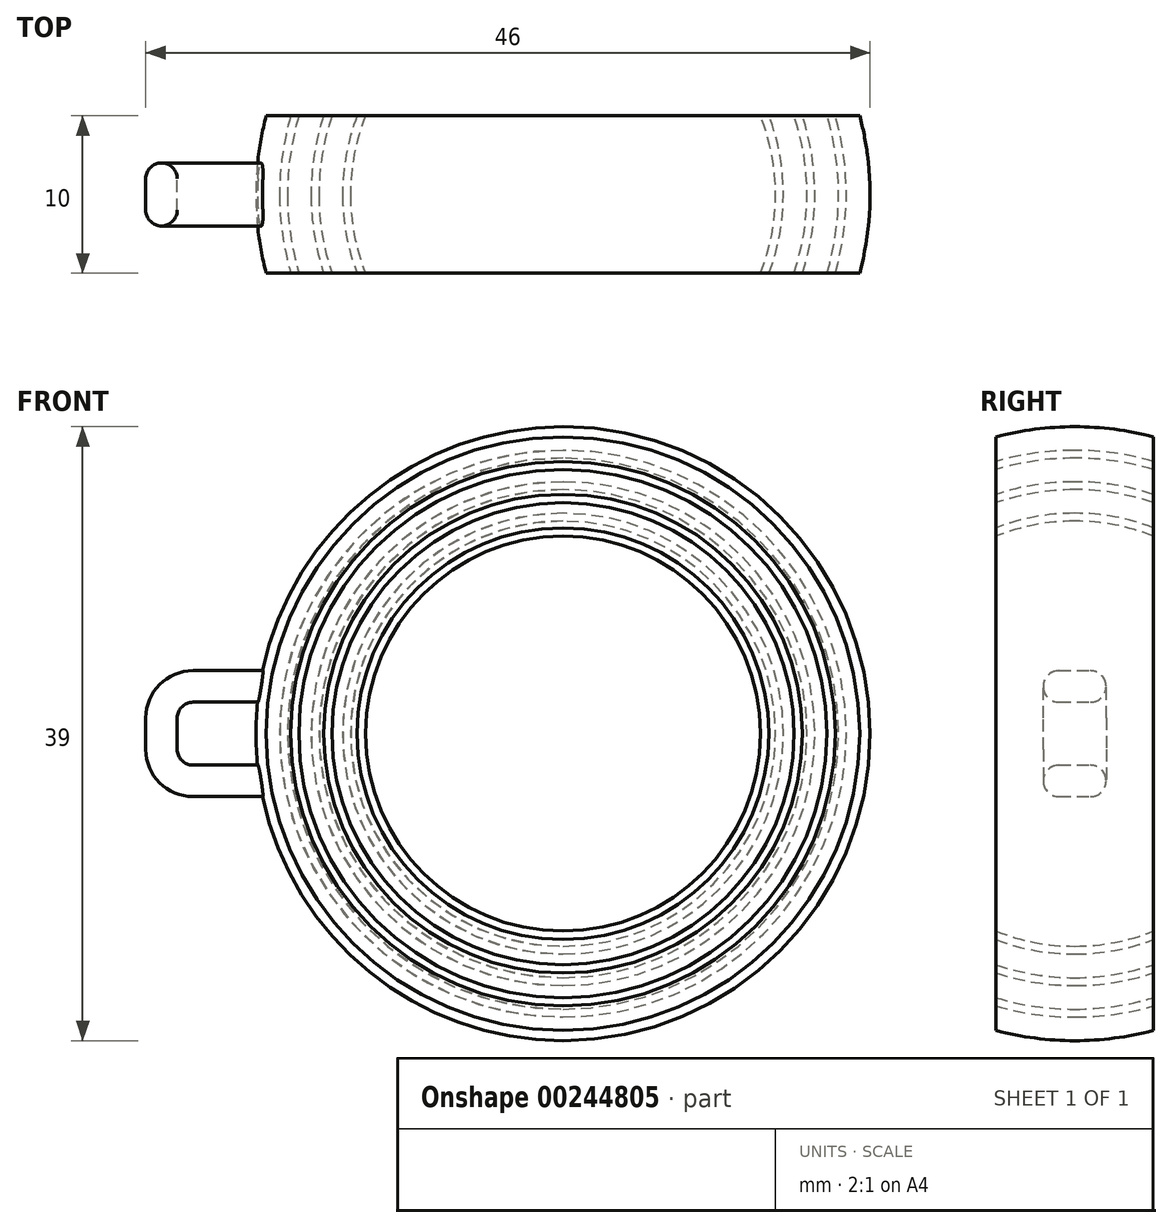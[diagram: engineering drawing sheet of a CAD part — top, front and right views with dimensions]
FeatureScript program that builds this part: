
annotation { "Feature Type Name" : "Feature", "Feature Type Description" : "" }
export const myFeature = defineFeature(function(context is Context, id is Id, definition is map)
    precondition{}
    {
        {
            var Q0;
            Q0=qCreatedBy(makeId("Front.planeOp"),FACE);
            var sketch = newSketch(context, id + "F0", { "sketchPlane" : qUnion([Q0])});
            skCircle(sketch, "E0", {"center": v(0, 0) * mm, "radius": 13.5 * mm});
            skCircle(sketch, "E1.0", {"center": v(0, 0) * mm, "radius": 14 * mm});
            skCircle(sketch, "E2.0", {"center": v(0, 0) * mm, "radius": 15.5 * mm});
            skCircle(sketch, "E3.0", {"center": v(0, 0) * mm, "radius": 16 * mm});
            skCircle(sketch, "E4.0", {"center": v(0, 0) * mm, "radius": 17.5 * mm});
            skCircle(sketch, "E5.0", {"center": v(0, 0) * mm, "radius": 18 * mm});
            skCircle(sketch, "E6.0", {"center": v(0, 0) * mm, "radius": 19.5 * mm});
            skLineSegment(sketch, "E7", {"start": v(0, 19.5) * mm, "end": v(0, -19.5) * mm});
            skSolve(sketch);
        }
        {
            var Q0;
            Q0=qCreatedBy(makeId("Top.planeOp"),FACE);
            var sketch = newSketch(context, id + "F1", { "sketchPlane" : qUnion([Q0])});
            skCircle(sketch, "E8", {"center": v(0, 0) * mm, "radius": 15 * mm});
            skSolve(sketch);
        }
        {
            var Q0;
            {var subQ0=sQuery(id+"F0.wireOp",EDGE,"E7");var subQ1=sQuery(id+"F0.wireOp",EDGE,"E0");var subQ2=makeQuery(id+"F0.imprint","INTERSECT",VERTEX,{"disambiguationData":[OD(0.0)],"derivedFrom":[subQ1,subQ0]});Q0=makeQuery(id+"F0.imprint","IMPRINT",FACE,{"disambiguationData":[TD([[makeQuery(id+"F0.imprint","IMPRINT",EDGE,{"disambiguationData":[TD([[subQ2,1.0]])],"derivedFrom":subQ1}),1.0]])]});}
            var Q1;
            {var subQ0=sQuery(id+"F0.wireOp",EDGE,"E7");var subQ1=sQuery(id+"F0.wireOp",EDGE,"E1.0");var subQ2=makeQuery(id+"F0.imprint","INTERSECT",VERTEX,{"disambiguationData":[OD(0.0)],"derivedFrom":[subQ1,subQ0]});Q1=makeQuery(id+"F0.imprint","IMPRINT",FACE,{"disambiguationData":[TD([[makeQuery(id+"F0.imprint","IMPRINT",EDGE,{"disambiguationData":[TD([[subQ2,1.0]])],"derivedFrom":subQ1}),-1.0]])]});}
            var Q2;
            {var subQ0=sQuery(id+"F0.wireOp",EDGE,"E7");var subQ1=sQuery(id+"F0.wireOp",EDGE,"E3.0");var subQ2=makeQuery(id+"F0.imprint","INTERSECT",VERTEX,{"disambiguationData":[OD(0.0)],"derivedFrom":[subQ1,subQ0]});Q2=makeQuery(id+"F0.imprint","IMPRINT",FACE,{"disambiguationData":[TD([[makeQuery(id+"F0.imprint","IMPRINT",EDGE,{"disambiguationData":[TD([[subQ2,1.0]])],"derivedFrom":subQ1}),-1.0]])]});}
            var Q3;
            {var subQ0=sQuery(id+"F0.wireOp",EDGE,"E7");var subQ1=sQuery(id+"F0.wireOp",EDGE,"E5.0");var subQ2=makeQuery(id+"F0.imprint","INTERSECT",VERTEX,{"disambiguationData":[OD(0.0)],"derivedFrom":[subQ1,subQ0]});Q3=makeQuery(id+"F0.imprint","IMPRINT",FACE,{"disambiguationData":[TD([[makeQuery(id+"F0.imprint","IMPRINT",EDGE,{"disambiguationData":[TD([[subQ2,1.0]])],"derivedFrom":subQ1}),-1.0]])]});}
            var Q4;
            Q4=sQuery(id+"F1.wireOp",EDGE,"E8");
            revolve(context, id + "F2", {"entities" : qUnion([Q0, Q1, Q2, Q3]), "axis" : qUnion([Q4]), "revolveType" : RevolveType.FULL});
        }
        {
            var Q0;
            Q0=qCreatedBy(makeId("Top.planeOp"),FACE);
            var sketch = newSketch(context, id + "F3", { "sketchPlane" : qUnion([Q0])});
            skPoint(sketch, "E9", {"position": v(0, 5) * mm});
            skPoint(sketch, "E10", {"position": v(0, -5) * mm});
            skLineSegment(sketch, "E11.bottom", {"start": v(-36.72, 5) * mm, "end": v(35.28, 5) * mm});
            skLineSegment(sketch, "E11.top", {"start": v(-36.72, 40.53) * mm, "end": v(35.28, 40.53) * mm});
            skLineSegment(sketch, "E11.left", {"start": v(-36.72, 5) * mm, "end": v(-36.72, 40.53) * mm});
            skLineSegment(sketch, "E11.right", {"start": v(35.28, 5) * mm, "end": v(35.28, 40.53) * mm});
            skLineSegment(sketch, "E12.MirrorCS", {"start": v(-36.72, -5) * mm, "end": v(-36.72, -40.53) * mm});
            skLineSegment(sketch, "E13.MirrorCS", {"start": v(-36.72, -40.53) * mm, "end": v(35.28, -40.53) * mm});
            skLineSegment(sketch, "E14.MirrorCS", {"start": v(-36.72, -5) * mm, "end": v(35.28, -5) * mm});
            skLineSegment(sketch, "E15.MirrorCS", {"start": v(35.28, -5) * mm, "end": v(35.28, -40.53) * mm});
            skSolve(sketch);
        }
        {
            var Q0;
            Q0=makeQuery(id+"F3.imprint","IMPRINT",FACE,{"disambiguationData":[TD([[makeQuery(id+"F3.imprint","IMPRINT",EDGE,{"derivedFrom":sQuery(id+"F3.wireOp",EDGE,"E11.bottom")}),1.0]])]});
            var Q1;
            Q1=makeQuery(id+"F3.imprint","IMPRINT",FACE,{"disambiguationData":[TD([[makeQuery(id+"F3.imprint","IMPRINT",EDGE,{"derivedFrom":sQuery(id+"F3.wireOp",EDGE,"E12.MirrorCS")}),1.0]])]});
            extrude(context, id + "F4", {"entities" : qUnion([Q0, Q1]), "operationType" : NewBodyOperationType.REMOVE, "oppositeDirection" : true, "depth" : 100 * mm, "hasSecondDirection" : true, "secondDirectionOppositeDirection" : false, "secondDirectionDepth" : 100 * mm});
        }
        {
            var Q0;
            Q0=qCreatedBy(makeId("Front.planeOp"),FACE);
            var sketch = newSketch(context, id + "F5", { "sketchPlane" : qUnion([Q0])});
            skLineSegment(sketch, "E16", {"start": v(-18.25, 2) * mm, "end": v(-24.5, 2) * mm});
            skLineSegment(sketch, "E17.0", {"start": v(-18.25, 4) * mm, "end": v(-26.5, 4) * mm});
            skLineSegment(sketch, "E18", {"start": v(-24.5, 2) * mm, "end": v(-24.5, 0) * mm});
            skLineSegment(sketch, "E19.0", {"start": v(-26.5, 4) * mm, "end": v(-26.5, 0) * mm});
            skLineSegment(sketch, "E20.MirrorCS", {"start": v(-26.5, -4) * mm, "end": v(-26.5, 0) * mm});
            skLineSegment(sketch, "E21.MirrorCS", {"start": v(-24.5, -2) * mm, "end": v(-24.5, 0) * mm});
            skLineSegment(sketch, "E22.MirrorCS", {"start": v(-18.25, -2) * mm, "end": v(-24.5, -2) * mm});
            skLineSegment(sketch, "E23.MirrorCS", {"start": v(-18.25, -4) * mm, "end": v(-26.5, -4) * mm});
            skLineSegment(sketch, "E24", {"start": v(-18.25, 4) * mm, "end": v(-18.25, -4) * mm});
            skSolve(sketch);
        }
        {
            var Q0;
            {var subQ4=sQuery(id+"F5.wireOp",EDGE,"E16");Q0=makeQuery(id+"F5.imprint","IMPRINT",FACE,{"disambiguationData":[TD([[makeQuery(id+"F5.imprint","IMPRINT",EDGE,{"derivedFrom":subQ4}),-1.0]])]});}
            extrude(context, id + "F6", {"entities" : qUnion([Q0]), "operationType" : NewBodyOperationType.ADD, "depth" : 2 * mm, "hasSecondDirection" : true, "secondDirectionOppositeDirection" : true, "secondDirectionDepth" : 2 * mm});
        }
        {
            var Q0;
            Q0=makeQuery(id+"F6.opExtrude","CAP_EDGE",EDGE,{"disambiguationData":[OSD([sQuery(id+"F5.wireOp",EDGE,"E17.0")])],"isStart":true});
            var Q1;
            Q1=makeQuery(id+"F6.opExtrude","CAP_EDGE",EDGE,{"disambiguationData":[OSD([sQuery(id+"F5.wireOp",EDGE,"E17.0")])],"isStart":false});
            var Q2;
            Q2=makeQuery(id+"F6.opExtrude","CAP_EDGE",EDGE,{"disambiguationData":[OSD([sQuery(id+"F5.wireOp",EDGE,"E19.0"),sQuery(id+"F5.wireOp",EDGE,"E20.MirrorCS")])],"isStart":true});
            var Q3;
            Q3=makeQuery(id+"F6.opExtrude","CAP_EDGE",EDGE,{"disambiguationData":[OSD([sQuery(id+"F5.wireOp",EDGE,"E19.0"),sQuery(id+"F5.wireOp",EDGE,"E20.MirrorCS")])],"isStart":false});
            var Q4;
            Q4=makeQuery(id+"F6.opExtrude","CAP_EDGE",EDGE,{"disambiguationData":[OSD([sQuery(id+"F5.wireOp",EDGE,"E23.MirrorCS")])],"isStart":true});
            var Q5;
            Q5=makeQuery(id+"F6.opExtrude","CAP_EDGE",EDGE,{"disambiguationData":[OSD([sQuery(id+"F5.wireOp",EDGE,"E23.MirrorCS")])],"isStart":false});
            var Q6;
            Q6=makeQuery(id+"F6.opExtrude","SWEPT_EDGE",EDGE,{"disambiguationData":[OSD([sQuery(id+"F5.wireOp",EDGE,"E16"),sQuery(id+"F5.wireOp",EDGE,"E18")])]});
            var Q7;
            Q7=makeQuery(id+"F6.opExtrude","SWEPT_EDGE",EDGE,{"disambiguationData":[OSD([sQuery(id+"F5.wireOp",EDGE,"E21.MirrorCS"),sQuery(id+"F5.wireOp",EDGE,"E22.MirrorCS")])]});
            var Q8;
            Q8=makeQuery(id+"F6.opExtrude","CAP_EDGE",EDGE,{"disambiguationData":[OSD([sQuery(id+"F5.wireOp",EDGE,"E18"),sQuery(id+"F5.wireOp",EDGE,"E21.MirrorCS")])],"isStart":true});
            var Q9;
            Q9=makeQuery(id+"F6.opExtrude","CAP_EDGE",EDGE,{"disambiguationData":[OSD([sQuery(id+"F5.wireOp",EDGE,"E22.MirrorCS")])],"isStart":true});
            var Q10;
            Q10=makeQuery(id+"F6.opExtrude","CAP_EDGE",EDGE,{"disambiguationData":[OSD([sQuery(id+"F5.wireOp",EDGE,"E16")])],"isStart":true});
            var Q11;
            Q11=makeQuery(id+"F6.opExtrude","CAP_EDGE",EDGE,{"disambiguationData":[OSD([sQuery(id+"F5.wireOp",EDGE,"E16")])],"isStart":false});
            var Q12;
            Q12=makeQuery(id+"F6.opExtrude","CAP_EDGE",EDGE,{"disambiguationData":[OSD([sQuery(id+"F5.wireOp",EDGE,"E18"),sQuery(id+"F5.wireOp",EDGE,"E21.MirrorCS")])],"isStart":false});
            var Q13;
            Q13=makeQuery(id+"F6.opExtrude","CAP_EDGE",EDGE,{"disambiguationData":[OSD([sQuery(id+"F5.wireOp",EDGE,"E22.MirrorCS")])],"isStart":false});
            fillet(context, id + "F7", {"entities" : qUnion([Q0, Q1, Q2, Q3, Q4, Q5, Q6, Q7, Q8, Q9, Q10, Q11, Q12, Q13]), "radius" : 1 * mm, "tangentPropagation" : true, "allowEdgeOverflow" : false});
        }
        {
            var Q0;
            Q0=makeQuery(id+"F6.opExtrude","SWEPT_EDGE",EDGE,{"disambiguationData":[OSD([sQuery(id+"F5.wireOp",EDGE,"E20.MirrorCS"),sQuery(id+"F5.wireOp",EDGE,"E23.MirrorCS")])]});
            var Q1;
            Q1=makeQuery(id+"F6.opExtrude","SWEPT_EDGE",EDGE,{"disambiguationData":[OSD([sQuery(id+"F5.wireOp",EDGE,"E17.0"),sQuery(id+"F5.wireOp",EDGE,"E19.0")])]});
            fillet(context, id + "F8", {"entities" : qUnion([Q0, Q1]), "radius" : 3 * mm, "tangentPropagation" : true, "allowEdgeOverflow" : false});
        }
    });
